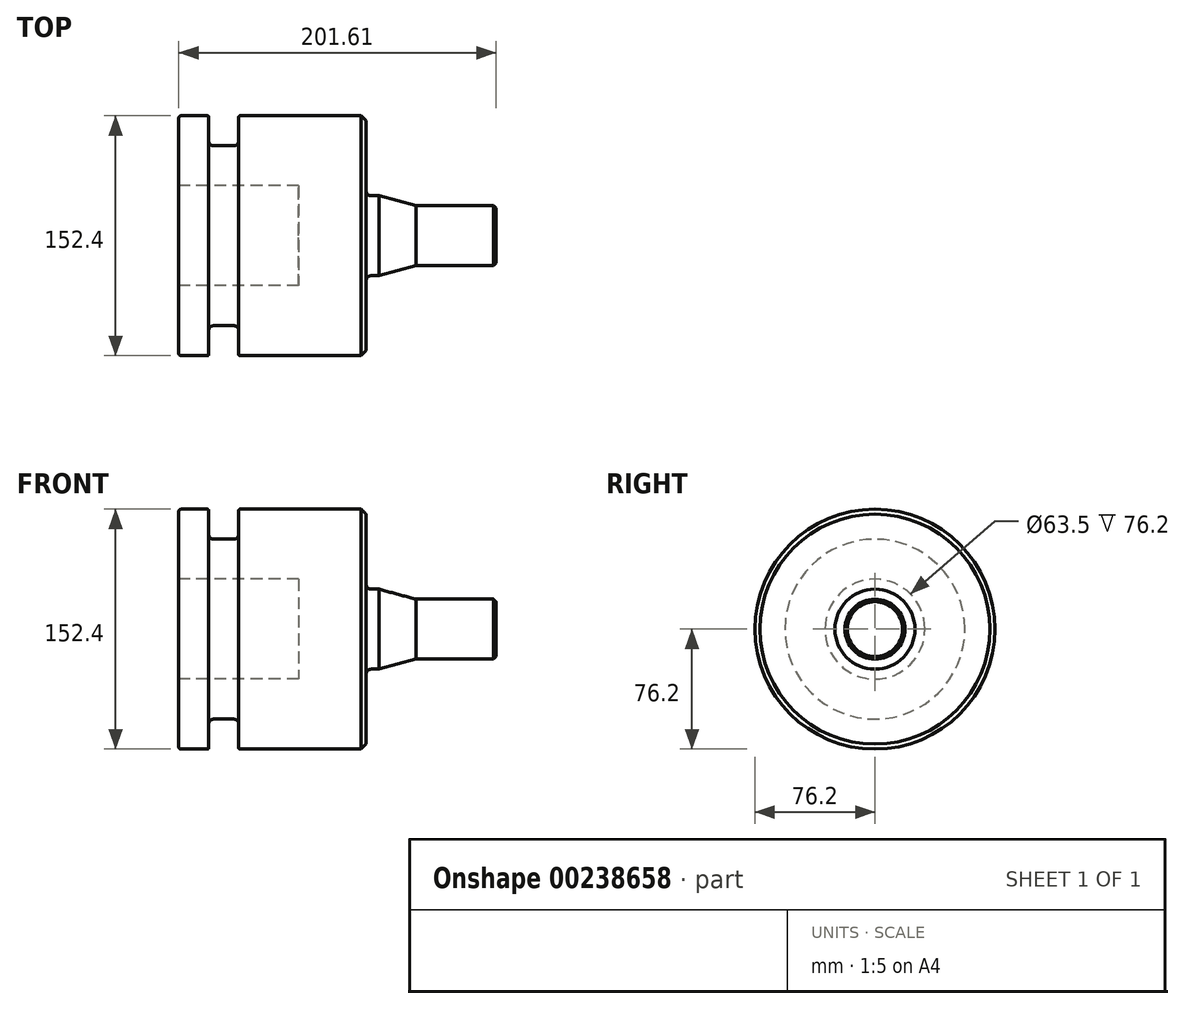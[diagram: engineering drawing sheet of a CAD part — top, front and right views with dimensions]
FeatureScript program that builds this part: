
annotation { "Feature Type Name" : "Feature", "Feature Type Description" : "" }
export const myFeature = defineFeature(function(context is Context, id is Id, definition is map)
    precondition{}
    {
        {
            var Q0;
            Q0=qCreatedBy(makeId("Front.planeOp"),FACE);
            var sketch = newSketch(context, id + "F0", { "sketchPlane" : qUnion([Q0])});
            skLineSegment(sketch, "E0", {"start": v(-203.2, 0) * mm, "end": v(0, 0) * mm});
            skLineSegment(sketch, "E1", {"start": v(0, 0) * mm, "end": v(0, -76.2) * mm});
            skLineSegment(sketch, "E2", {"start": v(-203.2, -76.2) * mm, "end": v(-203.2, 0) * mm});
            skLineSegment(sketch, "E3", {"start": v(0, -76.2) * mm, "end": v(-203.2, -76.2) * mm});
            skSolve(sketch);
        }
        {
            var Q0;
            Q0 = qSketchRegion(id + "F0", true);
            var Q1;
            Q1=sQuery(id+"F0.wireOp",EDGE,"E0");
            revolve(context, id + "F1", {"entities" : qUnion([Q0]), "axis" : qUnion([Q1]), "revolveType" : RevolveType.FULL});
        }
        {
            var Q0;
            Q0=qCreatedBy(makeId("Front.planeOp"),FACE);
            var sketch = newSketch(context, id + "F2", { "sketchPlane" : qUnion([Q0])});
            skLineSegment(sketch, "E4", {"start": v(0, 0) * mm, "end": v(0, 76.2) * mm});
            skLineSegment(sketch, "E5", {"start": v(-87.31, 76.2) * mm, "end": v(0, 76.2) * mm});
            skLineSegment(sketch, "E6", {"start": v(-87.31, 76.2) * mm, "end": v(-84.14, 73.03) * mm});
            skLineSegment(sketch, "E7", {"start": v(-84.14, 73.03) * mm, "end": v(-84.14, 25.4) * mm});
            skLineSegment(sketch, "E8", {"start": v(-84.14, 25.4) * mm, "end": v(-76.09, 25.4) * mm});
            skLineSegment(sketch, "E9", {"start": v(-76.09, 25.4) * mm, "end": v(-52.39, 19.05) * mm});
            skLineSegment(sketch, "E10", {"start": v(-52.39, 19.05) * mm, "end": v(-3.18, 19.05) * mm});
            skLineSegment(sketch, "E11", {"start": v(-3.18, 19.05) * mm, "end": v(-1.59, 17.46) * mm});
            skLineSegment(sketch, "E12", {"start": v(-1.59, 17.46) * mm, "end": v(-1.59, 0) * mm});
            skLineSegment(sketch, "E13", {"start": v(-1.59, 0) * mm, "end": v(0, 0) * mm});
            skLineSegment(sketch, "E14", {"start": v(9.23, 0) * mm, "end": v(-160.3, 0) * mm});
            skSolve(sketch);
        }
        {
            var Q0;
            Q0 = qSketchRegion(id + "F2", true);
            var Q1;
            Q1=sQuery(id+"F2.wireOp",EDGE,"E14");
            revolve(context, id + "F3", {"operationType" : NewBodyOperationType.REMOVE, "entities" : qUnion([Q0]), "axis" : qUnion([Q1]), "revolveType" : RevolveType.FULL, "oppositeDirection" : true});
        }
        {
            var Q0;
            Q0=makeQuery(id+"F1.opRevolve","SWEPT_FACE",FACE,{"disambiguationData":[OSD([sQuery(id+"F0.wireOp",EDGE,"E2")])]});
            var sketch = newSketch(context, id + "F4", { "sketchPlane" : qUnion([Q0])});
            skCircle(sketch, "E15", {"center": v(0, 0) * mm, "radius": 31.75 * mm});
            skSolve(sketch);
        }
        {
            var Q0;
            Q0 = qSketchRegion(id + "F4", true);
            extrude(context, id + "F5", {"entities" : qUnion([Q0]), "operationType" : NewBodyOperationType.REMOVE, "oppositeDirection" : true, "depth" : 76.2 * mm});
        }
        {
            var Q0;
            Q0=makeQuery(id+"F5.boolean.opBoolean","COPY",EDGE,{"derivedFrom":makeQuery(id+"F5.opExtrude","CAP_EDGE",EDGE,{"disambiguationData":[OSD([sQuery(id+"F4.wireOp",EDGE,"E15")])],"isStart":true})});
            var Q1;
            Q1=makeQuery(id+"F1.opRevolve","SWEPT_EDGE",EDGE,{"disambiguationData":[OSD([sQuery(id+"F0.wireOp",EDGE,"E2"),sQuery(id+"F0.wireOp",EDGE,"E3")])]});
            var Q2;
            Q2=makeQuery(id+"F3.boolean.opBoolean","COPY",EDGE,{"derivedFrom":makeQuery(id+"F3.opRevolve","SWEPT_EDGE",EDGE,{"disambiguationData":[OSD([sQuery(id+"F2.wireOp",EDGE,"E5"),sQuery(id+"F2.wireOp",EDGE,"E6")])]})});
            fillet(context, id + "F6", {"entities" : qUnion([Q0, Q1, Q2]), "radius" : 1.59 * mm, "tangentPropagation" : true, "allowEdgeOverflow" : false});
        }
        {
            var Q0;
            Q0=makeQuery(id+"F3.boolean.opBoolean","COPY",EDGE,{"derivedFrom":makeQuery(id+"F3.opRevolve","SWEPT_EDGE",EDGE,{"disambiguationData":[OSD([sQuery(id+"F2.wireOp",EDGE,"E7"),sQuery(id+"F2.wireOp",EDGE,"E8")])]})});
            fillet(context, id + "F7", {"entities" : qUnion([Q0]), "radius" : 3.17 * mm, "tangentPropagation" : true, "allowEdgeOverflow" : false});
        }
        {
            var Q0;
            Q0=qCreatedBy(makeId("Front.planeOp"),FACE);
            var sketch = newSketch(context, id + "F8", { "sketchPlane" : qUnion([Q0])});
            skLineSegment(sketch, "E16", {"start": v(-184.15, 80.05) * mm, "end": v(-184.15, 60.32) * mm});
            skLineSegment(sketch, "E17", {"start": v(-180.97, 57.15) * mm, "end": v(-168.28, 57.15) * mm});
            skLineSegment(sketch, "E18", {"start": v(-165.1, 60.32) * mm, "end": v(-165.1, 80.05) * mm});
            skPoint(sketch, "E19.visualSharp", {"position": v(-184.15, 57.15) * mm});
            skArc(sketch, "E19.filletArc", {"start": v(-184.15, 60.32) * mm, "mid": v(-183.22, 58.08) * mm, "end": v(-180.97, 57.15) * mm});
            skPoint(sketch, "E20.visualSharp", {"position": v(-165.1, 57.15) * mm});
            skArc(sketch, "E20.filletArc", {"start": v(-168.28, 57.15) * mm, "mid": v(-166.03, 58.08) * mm, "end": v(-165.1, 60.32) * mm});
            skLineSegment(sketch, "E21", {"start": v(22.76, 0) * mm, "end": v(-241.98, 0) * mm, "construction": true});
            skLineSegment(sketch, "E22", {"start": v(-184.15, 80.05) * mm, "end": v(-165.1, 80.05) * mm});
            skSolve(sketch);
        }
        {
            var Q0;
            Q0 = qSketchRegion(id + "F8", true);
            var Q1;
            Q1=makeQuery(id+"F3.boolean.opBoolean","COPY",FACE,{"derivedFrom":makeQuery(id+"F3.opRevolve","SWEPT_FACE",FACE,{"disambiguationData":[OSD([sQuery(id+"F2.wireOp",EDGE,"E10")])]})});
            revolve(context, id + "F9", {"operationType" : NewBodyOperationType.REMOVE, "entities" : qUnion([Q0]), "axis" : qUnion([Q1]), "revolveType" : RevolveType.FULL});
        }
        {
            var Q0;
            Q0=makeQuery(id+"F9.boolean.opBoolean","INTERSECT",EDGE,{"derivedFrom":[makeQuery(id+"F1.opRevolve","SWEPT_FACE",FACE,{"disambiguationData":[OSD([sQuery(id+"F0.wireOp",EDGE,"E3")])]}),makeQuery(id+"F9.opRevolve","SWEPT_FACE",FACE,{"disambiguationData":[OSD([sQuery(id+"F8.wireOp",EDGE,"E18")])]})]});
            var Q1;
            Q1=makeQuery(id+"F9.boolean.opBoolean","INTERSECT",EDGE,{"derivedFrom":[makeQuery(id+"F1.opRevolve","SWEPT_FACE",FACE,{"disambiguationData":[OSD([sQuery(id+"F0.wireOp",EDGE,"E3")])]}),makeQuery(id+"F9.opRevolve","SWEPT_FACE",FACE,{"disambiguationData":[OSD([sQuery(id+"F8.wireOp",EDGE,"E16")])]})]});
            fillet(context, id + "F10", {"entities" : qUnion([Q0, Q1]), "radius" : 0.8 * mm, "tangentPropagation" : true, "allowEdgeOverflow" : false});
        }
    });
